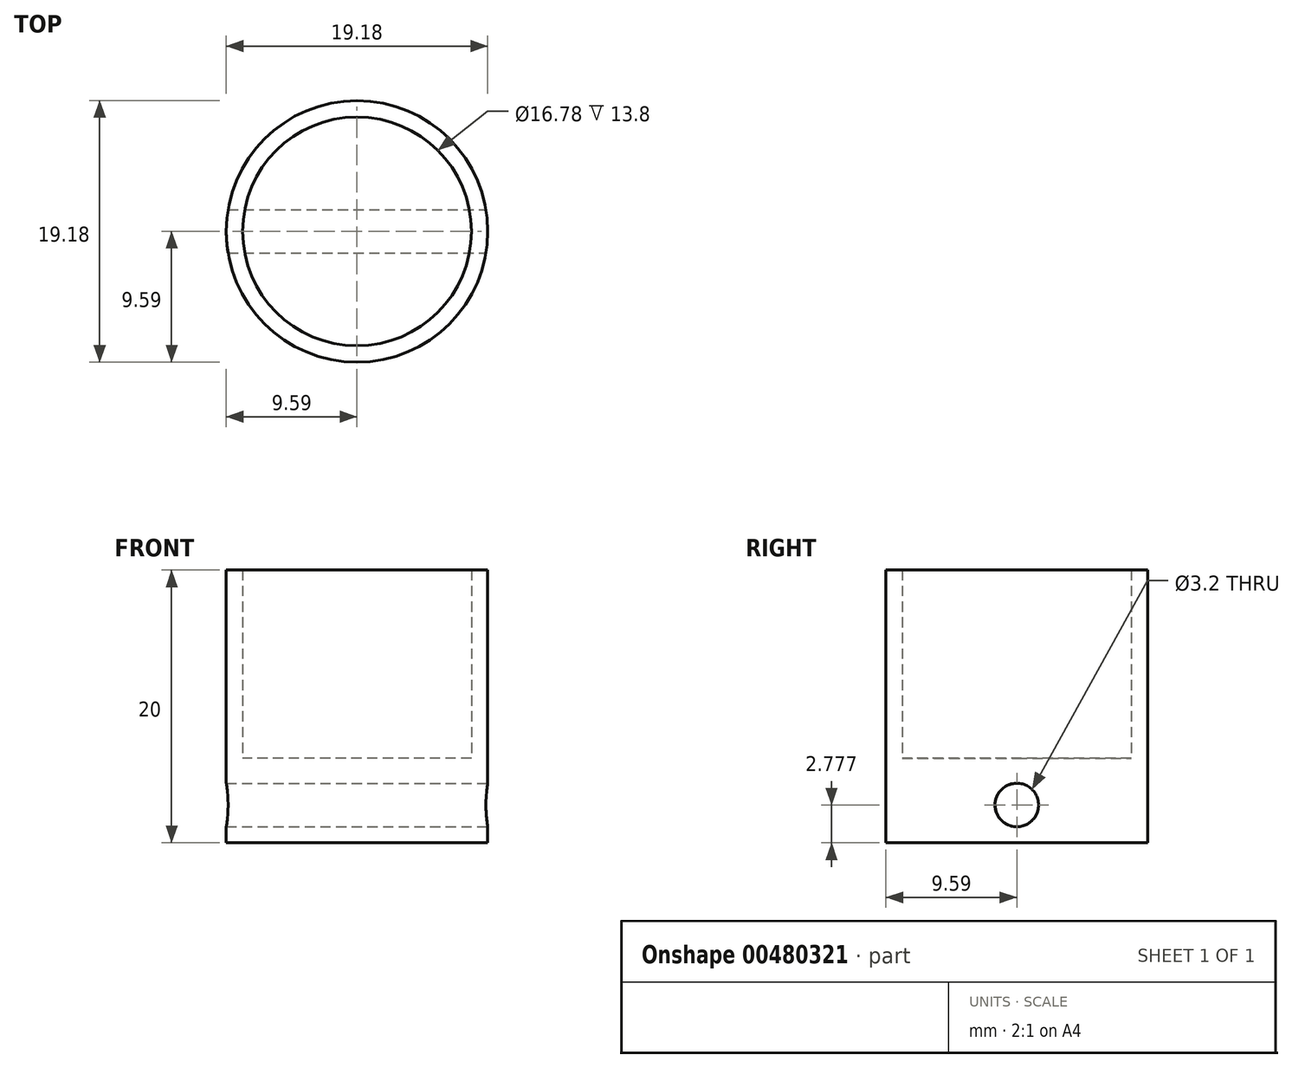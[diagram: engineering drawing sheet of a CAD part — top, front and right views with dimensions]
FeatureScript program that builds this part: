
annotation { "Feature Type Name" : "Feature", "Feature Type Description" : "" }
export const myFeature = defineFeature(function(context is Context, id is Id, definition is map)
    precondition{}
    {
        {
            var Q0;
            Q0=qCreatedBy(makeId("Top.planeOp"),FACE);
            var sketch = newSketch(context, id + "F0", { "sketchPlane" : qUnion([Q0])});
            skCircle(sketch, "E0", {"center": v(0, 0) * mm, "radius": 8.39 * mm});
            skCircle(sketch, "E1.0", {"center": v(0, 0) * mm, "radius": 9.59 * mm});
            skSolve(sketch);
        }
        {
            var Q0;
            Q0=makeQuery(id+"F0.imprint","IMPRINT",FACE,{"disambiguationData":[TD([[makeQuery(id+"F0.imprint","IMPRINT",EDGE,{"derivedFrom":sQuery(id+"F0.wireOp",EDGE,"E0")}),-1.0]])]});
            extrude(context, id + "F1", {"entities" : qUnion([Q0]), "depth" : 15 * mm, "offsetDistance" : 25 * mm});
        }
        {
            var Q0;
            Q0=makeQuery(id+"F0.imprint","IMPRINT",FACE,{"disambiguationData":[TD([[makeQuery(id+"F0.imprint","IMPRINT",EDGE,{"derivedFrom":sQuery(id+"F0.wireOp",EDGE,"E0")}),1.0]])]});
            extrude(context, id + "F2", {"entities" : qUnion([Q0]), "operationType" : NewBodyOperationType.ADD, "depth" : 1.2 * mm, "offsetDistance" : 25 * mm});
        }
        {
            var Q0;
            Q0=makeQuery(id+"F0.imprint","IMPRINT",FACE,{"disambiguationData":[TD([[makeQuery(id+"F0.imprint","IMPRINT",EDGE,{"derivedFrom":sQuery(id+"F0.wireOp",EDGE,"E0")}),1.0]])]});
            var sketch = newSketch(context, id + "F3", { "sketchPlane" : qUnion([Q0])});
            skLineSegment(sketch, "E2", {"start": v(0, 0) * mm, "end": v(0, -6.95) * mm, "construction": true});
            skLineSegment(sketch, "E3.bottom", {"start": v(-5.68, -3) * mm, "end": v(-3.68, -3) * mm});
            skLineSegment(sketch, "E3.top", {"start": v(-5.68, 3) * mm, "end": v(-3.68, 3) * mm});
            skLineSegment(sketch, "E3.left", {"start": v(-5.68, -3) * mm, "end": v(-5.68, 3) * mm});
            skLineSegment(sketch, "E3.right", {"start": v(-3.68, -3) * mm, "end": v(-3.68, 3) * mm});
            skPoint(sketch, "E3.middle", {"position": v(-4.68, 0) * mm});
            skLineSegment(sketch, "E4.MirrorCS", {"start": v(5.68, -3) * mm, "end": v(3.68, -3) * mm});
            skLineSegment(sketch, "E5.MirrorCS", {"start": v(5.68, -3) * mm, "end": v(5.68, 3) * mm});
            skPoint(sketch, "E6.MirrorP", {"position": v(4.68, 0) * mm});
            skLineSegment(sketch, "E7.MirrorCS", {"start": v(3.68, -3) * mm, "end": v(3.68, 3) * mm});
            skLineSegment(sketch, "E8.MirrorCS", {"start": v(5.68, 3) * mm, "end": v(3.68, 3) * mm});
            skSolve(sketch);
        }
        {
            var Q0;
            Q0=makeQuery(id+"F3.imprint","IMPRINT",FACE,{"disambiguationData":[TD([[makeQuery(id+"F3.imprint","IMPRINT",EDGE,{"derivedFrom":sQuery(id+"F3.wireOp",EDGE,"E3.bottom")}),1.0]])]});
            var Q1;
            Q1=makeQuery(id+"F3.imprint","IMPRINT",FACE,{"disambiguationData":[TD([[makeQuery(id+"F3.imprint","IMPRINT",EDGE,{"derivedFrom":sQuery(id+"F3.wireOp",EDGE,"E5.MirrorCS")}),1.0]])]});
            extrude(context, id + "F4", {"entities" : qUnion([Q0, Q1]), "operationType" : NewBodyOperationType.ADD, "oppositeDirection" : true, "depth" : 5 * mm, "offsetDistance" : 25 * mm});
        }
        {
            var Q0;
            Q0=makeQuery(id+"F4.opExtrude","SWEPT_FACE",FACE,{"disambiguationData":[OSD([sQuery(id+"F3.wireOp",EDGE,"E5.MirrorCS")])]});
            var sketch = newSketch(context, id + "F5", { "sketchPlane" : qUnion([Q0])});
            skCircle(sketch, "E9", {"center": v(0, -2.22) * mm, "radius": 1.6 * mm});
            skSolve(sketch);
        }
        {
            var Q0;
            Q0=makeQuery(id+"F5.imprint","IMPRINT",FACE,{"disambiguationData":[TD([[makeQuery(id+"F5.imprint","IMPRINT",EDGE,{"derivedFrom":sQuery(id+"F5.wireOp",EDGE,"E9")}),1.0]])]});
            extrude(context, id + "F6", {"entities" : qUnion([Q0]), "operationType" : NewBodyOperationType.REMOVE, "endBound" : BoundingType.THROUGH_ALL, "oppositeDirection" : true, "depth" : 25 * mm, "offsetDistance" : 25 * mm});
        }
        {
            var Q0;
            Q0=makeQuery(id+"F0.imprint","IMPRINT",FACE,{"disambiguationData":[TD([[makeQuery(id+"F0.imprint","IMPRINT",EDGE,{"derivedFrom":sQuery(id+"F0.wireOp",EDGE,"E0")}),1.0]])]});
            extrude(context, id + "F7", {"entities" : qUnion([Q0]), "operationType" : NewBodyOperationType.ADD, "oppositeDirection" : true, "depth" : 5 * mm, "offsetDistance" : 25 * mm});
        }
        {
            var Q0;
            Q0=makeQuery(id+"F0.imprint","IMPRINT",FACE,{"disambiguationData":[TD([[makeQuery(id+"F0.imprint","IMPRINT",EDGE,{"derivedFrom":sQuery(id+"F0.wireOp",EDGE,"E0")}),-1.0]])]});
            extrude(context, id + "F8", {"entities" : qUnion([Q0]), "operationType" : NewBodyOperationType.ADD, "oppositeDirection" : true, "depth" : 5 * mm, "offsetDistance" : 25 * mm});
        }
        {
            var Q0;
            Q0 = qSketchRegion(id + "F5", true);
            extrude(context, id + "F9", {"entities" : qUnion([Q0]), "operationType" : NewBodyOperationType.REMOVE, "oppositeDirection" : true, "depth" : 79.4 * mm, "offsetDistance" : 25 * mm, "symmetric" : true});
        }
    });
